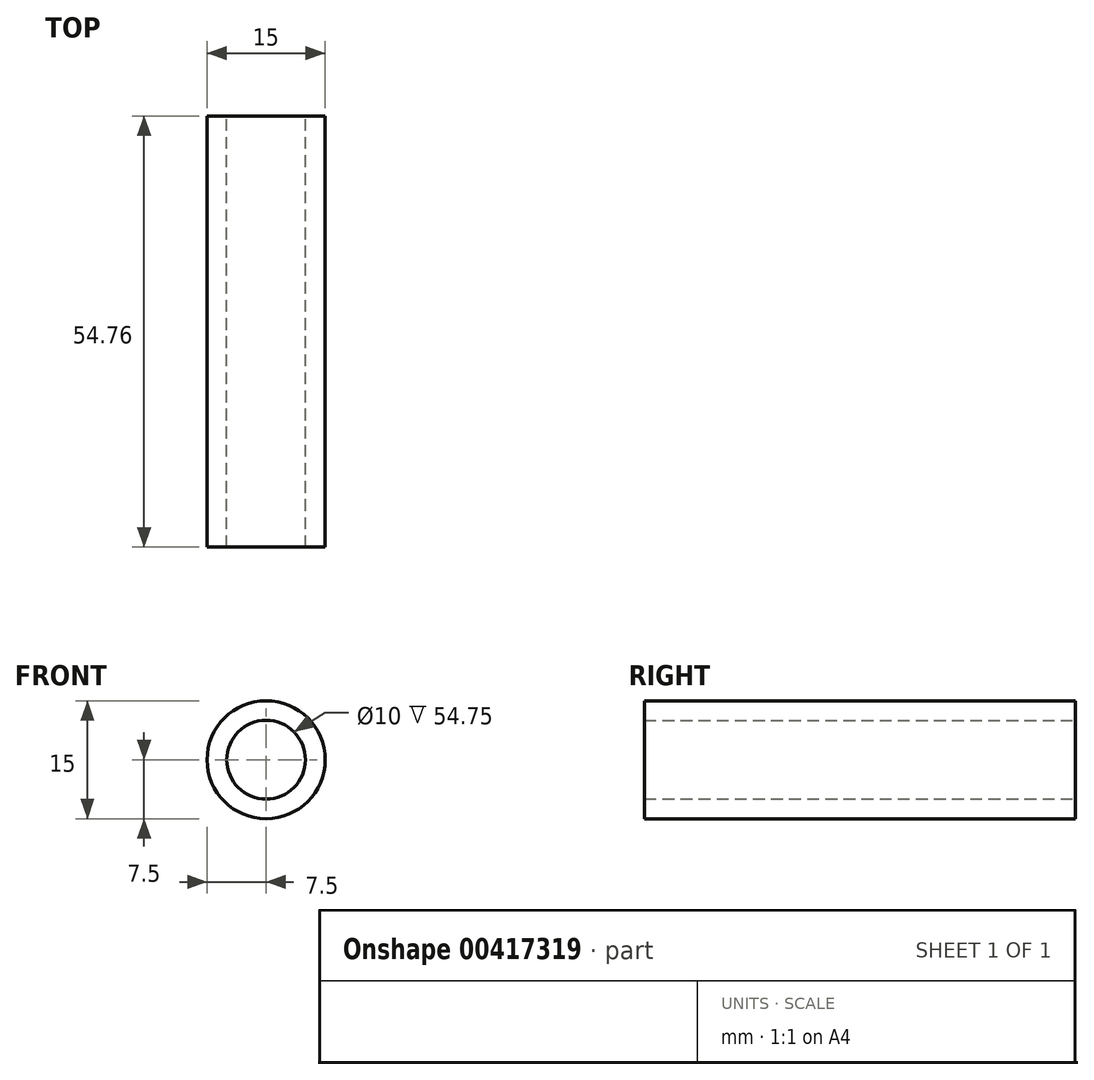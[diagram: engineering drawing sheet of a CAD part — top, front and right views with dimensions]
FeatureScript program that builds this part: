
annotation { "Feature Type Name" : "Feature", "Feature Type Description" : "" }
export const myFeature = defineFeature(function(context is Context, id is Id, definition is map)
    precondition{}
    {
        {
            var Q0;
            Q0=qCreatedBy(makeId("Front.planeOp"),FACE);
            var sketch = newSketch(context, id + "F0", { "sketchPlane" : qUnion([Q0])});
            skCircle(sketch, "E0", {"center": v(0, 0) * mm, "radius": 7.5 * mm});
            skCircle(sketch, "E1", {"center": v(0, 0) * mm, "radius": 5 * mm});
            skSolve(sketch);
        }
        {
            var Q0;
            Q0 = qSketchRegion(id + "F0", true);
            extrude(context, id + "F1", {"entities" : qUnion([Q0]), "endBound" : BoundingType.SYMMETRIC, "depth" : 54.75 * mm});
        }
    });
